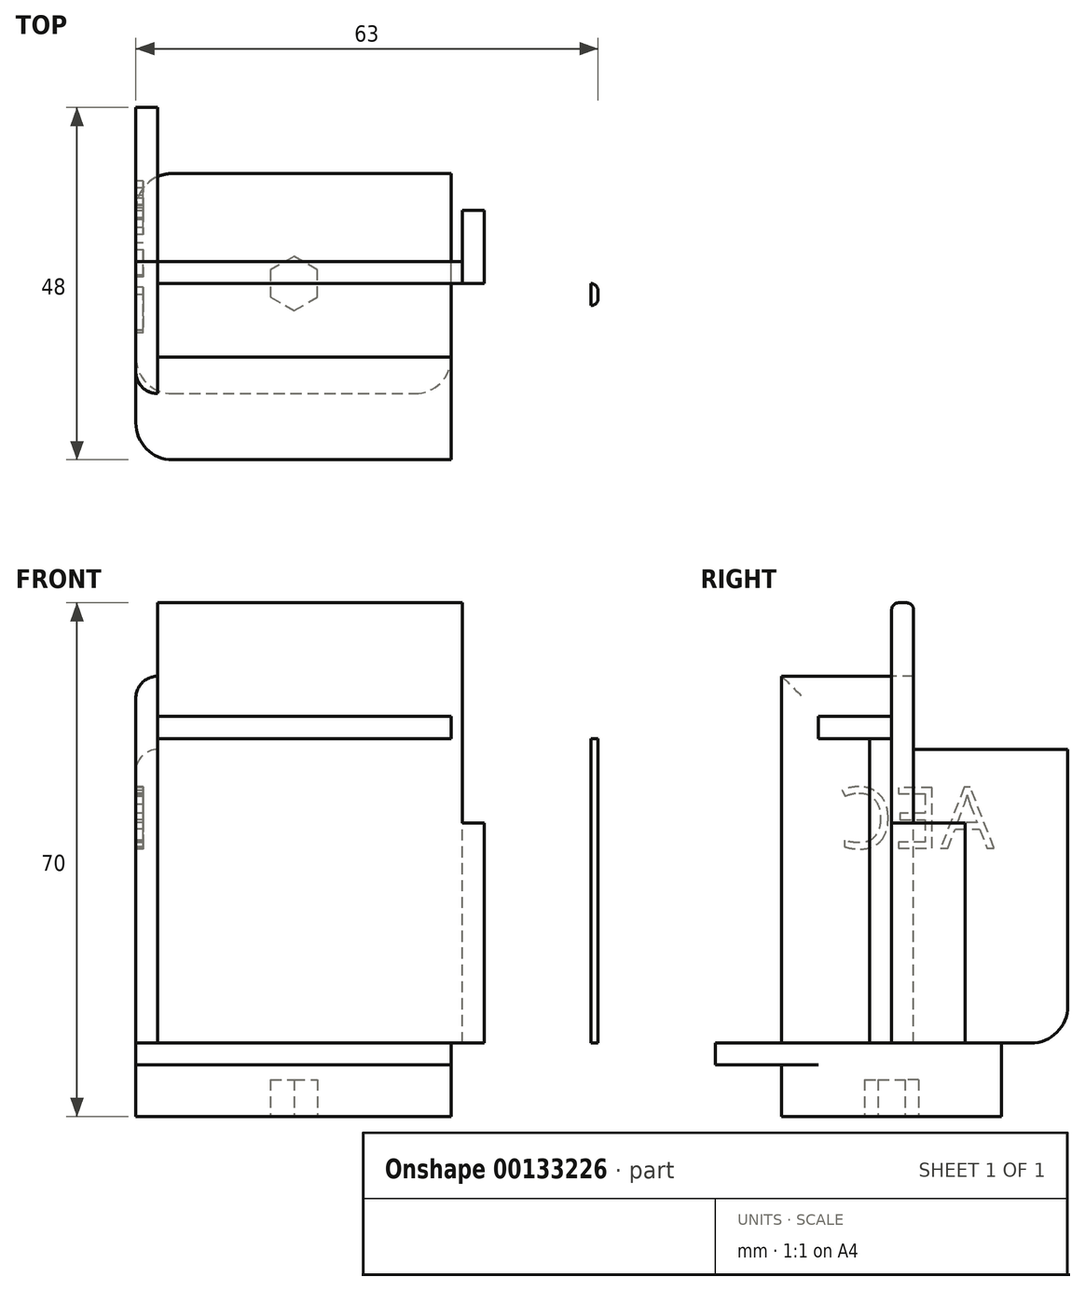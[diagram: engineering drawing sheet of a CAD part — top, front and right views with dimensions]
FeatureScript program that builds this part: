
annotation { "Feature Type Name" : "Feature", "Feature Type Description" : "" }
export const myFeature = defineFeature(function(context is Context, id is Id, definition is map)
    precondition{}
    {
        {
            var Q0;
            Q0=qCreatedBy(makeId("Front.planeOp"),FACE);
            var sketch = newSketch(context, id + "F0", { "sketchPlane" : qUnion([Q0])});
            skLineSegment(sketch, "E0.bottom", {"start": v(0, 0) * mm, "end": v(60, 0) * mm});
            skLineSegment(sketch, "E0.top", {"start": v(0, 41.5) * mm, "end": v(60, 41.5) * mm});
            skLineSegment(sketch, "E0.left", {"start": v(0, 0) * mm, "end": v(0, 41.5) * mm});
            skLineSegment(sketch, "E0.right", {"start": v(60, 0) * mm, "end": v(60, 41.5) * mm});
            skSolve(sketch);
        }
        {
            var Q0;
            Q0=makeQuery(id+"F0.imprint","IMPRINT",FACE,{"disambiguationData":[TD([[makeQuery(id+"F0.imprint","IMPRINT",EDGE,{"derivedFrom":sQuery(id+"F0.wireOp",EDGE,"E0.bottom")}),1.0]])]});
            extrude(context, id + "F1", {"entities" : qUnion([Q0]), "depth" : 3 * mm});
        }
        {
            var Q0;
            Q0=makeQuery(id+"F1.opExtrude","CAP_FACE",FACE,{"disambiguationData":[OSD([sQuery(id+"F0.wireOp",EDGE,"E0.bottom"),sQuery(id+"F0.wireOp",EDGE,"E0.top"),sQuery(id+"F0.wireOp",EDGE,"E0.left"),sQuery(id+"F0.wireOp",EDGE,"E0.right")])],"isStart":true});
            var sketch = newSketch(context, id + "F2", { "sketchPlane" : qUnion([Q0])});
            skLineSegment(sketch, "E1.bottom", {"start": v(0, 0) * mm, "end": v(-41.5, 0) * mm});
            skLineSegment(sketch, "E1.top", {"start": v(0, 60) * mm, "end": v(-41.5, 60) * mm});
            skLineSegment(sketch, "E1.left", {"start": v(0, 0) * mm, "end": v(0, 60) * mm});
            skLineSegment(sketch, "E1.right", {"start": v(-41.5, 0) * mm, "end": v(-41.5, 60) * mm});
            skSolve(sketch);
        }
        {
            var Q0;
            {var subQ0=sQuery(id+"F2.wireOp",EDGE,"E1.top");Q0=makeQuery(id+"F2.imprint","IMPRINT",FACE,{"disambiguationData":[TD([[makeQuery(id+"F2.imprint","IMPRINT",EDGE,{"derivedFrom":subQ0}),1.0]])]});}
            var Q1;
            {var subQ0=sQuery(id+"F2.wireOp",EDGE,"E1.bottom");Q1=makeQuery(id+"F2.imprint","IMPRINT",FACE,{"disambiguationData":[TD([[makeQuery(id+"F2.imprint","IMPRINT",EDGE,{"derivedFrom":subQ0}),-1.0]])]});}
            extrude(context, id + "F3", {"entities" : qUnion([Q0, Q1]), "operationType" : NewBodyOperationType.ADD, "depth" : 3 * mm});
        }
        {
            var Q0;
            Q0=makeQuery(id+"F3.boolean.opBoolean","MERGE",FACE,{"derivedFrom":[makeQuery(id+"F1.opExtrude","SWEPT_FACE",FACE,{"disambiguationData":[OSD([sQuery(id+"F0.wireOp",EDGE,"E0.left")])]}),makeQuery(id+"F3.opExtrude","SWEPT_FACE",FACE,{"disambiguationData":[OSD([sQuery(id+"F2.wireOp",EDGE,"E1.left")])]})]});
            var sketch = newSketch(context, id + "F4", { "sketchPlane" : qUnion([Q0])});
            skLineSegment(sketch, "E2", {"start": v(0, 0) * mm, "end": v(-15, 0) * mm, "construction": true});
            skLineSegment(sketch, "E3", {"start": v(-15, 0) * mm, "end": v(15, 0) * mm, "construction": true});
            skLineSegment(sketch, "E4", {"start": v(15, 0) * mm, "end": v(15, 50) * mm, "construction": true});
            skLineSegment(sketch, "E5.bottom", {"start": v(-15, 0) * mm, "end": v(15, 0) * mm});
            skLineSegment(sketch, "E5.top", {"start": v(-15, 50) * mm, "end": v(15, 50) * mm});
            skLineSegment(sketch, "E5.left", {"start": v(-15, 0) * mm, "end": v(-15, 50) * mm});
            skLineSegment(sketch, "E5.right", {"start": v(15, 0) * mm, "end": v(15, 50) * mm});
            skSolve(sketch);
        }
        {
            var Q0;
            {var subQ3=sQuery(id+"F4.wireOp",EDGE,"E5.left");Q0=makeQuery(id+"F4.imprint","IMPRINT",FACE,{"disambiguationData":[TD([[makeQuery(id+"F4.imprint","IMPRINT",EDGE,{"derivedFrom":subQ3}),-1.0]])]});}
            var Q1;
            {var subQ2=sQuery(id+"F4.wireOp",EDGE,"E5.right");Q1=makeQuery(id+"F4.imprint","IMPRINT",FACE,{"disambiguationData":[TD([[makeQuery(id+"F4.imprint","IMPRINT",EDGE,{"derivedFrom":subQ2}),1.0]])]});}
            var Q2;
            {var subQ0=sQuery(id+"F0.wireOp",EDGE,"E0.left");var subQ1=makeQuery(id+"F1.opExtrude","CAP_EDGE",EDGE,{"disambiguationData":[OSD([subQ0])],"isStart":false});Q2=makeQuery(id+"F4.imprint","IMPRINT",FACE,{"disambiguationData":[TD([[makeQuery(id+"F4.imprint","IMPRINT",EDGE,{"derivedFrom":subQ1}),1.0]])]});}
            extrude(context, id + "F5", {"entities" : qUnion([Q0, Q1, Q2]), "operationType" : NewBodyOperationType.ADD, "depth" : 3 * mm});
        }
        {
            var Q0;
            Q0=makeQuery(id+"F5.boolean.opBoolean","MERGE",FACE,{"derivedFrom":[makeQuery(id+"F3.boolean.opBoolean","MERGE",FACE,{"derivedFrom":[makeQuery(id+"F1.opExtrude","SWEPT_FACE",FACE,{"disambiguationData":[OSD([sQuery(id+"F0.wireOp",EDGE,"E0.bottom")])]}),makeQuery(id+"F3.opExtrude","SWEPT_FACE",FACE,{"disambiguationData":[OSD([sQuery(id+"F2.wireOp",EDGE,"E1.bottom")])]})]}),makeQuery(id+"F5.opExtrude","SWEPT_FACE",FACE,{"disambiguationData":[OSD([sQuery(id+"F4.wireOp",EDGE,"E5.bottom")])]})]});
            var sketch = newSketch(context, id + "F6", { "sketchPlane" : qUnion([Q0])});
            skLineSegment(sketch, "E6.bottom", {"start": v(-3, 15) * mm, "end": v(47, 15) * mm});
            skLineSegment(sketch, "E6.top", {"start": v(-3, -15) * mm, "end": v(47, -15) * mm});
            skLineSegment(sketch, "E6.left", {"start": v(-3, 15) * mm, "end": v(-3, -15) * mm});
            skLineSegment(sketch, "E6.right", {"start": v(47, 15) * mm, "end": v(47, -15) * mm});
            skSolve(sketch);
        }
        {
            var Q0;
            {var subQ0=sQuery(id+"F6.wireOp",EDGE,"E6.bottom");var subQ5=sQuery(id+"F6.wireOp",EDGE,"E6.right");var subQ6=makeQuery(id+"F6.imprint","INTERSECT",VERTEX,{"derivedFrom":[subQ0,subQ5]});Q0=makeQuery(id+"F6.imprint","IMPRINT",FACE,{"disambiguationData":[TD([[makeQuery(id+"F6.imprint","IMPRINT",EDGE,{"disambiguationData":[TD([[subQ6,-1.0]])],"derivedFrom":subQ5}),-1.0]])]});}
            var Q1;
            {var subQ0=sQuery(id+"F2.wireOp",EDGE,"E1.bottom");Q1=makeQuery(id+"F6.imprint","IMPRINT",FACE,{"disambiguationData":[TD([[makeQuery(id+"F6.imprint","IMPRINT",EDGE,{"derivedFrom":makeQuery(id+"F3.opExtrude","CAP_EDGE",EDGE,{"disambiguationData":[OSD([subQ0])],"isStart":false})}),-1.0]])]});}
            var Q2;
            {var subQ6=sQuery(id+"F6.wireOp",EDGE,"E6.left");Q2=makeQuery(id+"F6.imprint","IMPRINT",FACE,{"disambiguationData":[TD([[makeQuery(id+"F6.imprint","IMPRINT",EDGE,{"derivedFrom":subQ6}),-1.0]])]});}
            extrude(context, id + "F7", {"entities" : qUnion([Q0, Q1, Q2]), "operationType" : NewBodyOperationType.ADD, "depth" : 10 * mm});
        }
        {
            var Q0;
            Q0=makeQuery(id+"F7.boolean.opBoolean","MERGE",FACE,{"derivedFrom":[makeQuery(id+"F5.opExtrude","SWEPT_FACE",FACE,{"disambiguationData":[OSD([sQuery(id+"F4.wireOp",EDGE,"E5.right")])]}),makeQuery(id+"F7.opExtrude","SWEPT_FACE",FACE,{"disambiguationData":[OSD([sQuery(id+"F6.wireOp",EDGE,"E6.bottom")])]})]});
            var sketch = newSketch(context, id + "F8", { "sketchPlane" : qUnion([Q0])});
            skLineSegment(sketch, "E7.bottom", {"start": v(-3, 0) * mm, "end": v(47, 0) * mm});
            skLineSegment(sketch, "E7.top", {"start": v(-3, -3) * mm, "end": v(47, -3) * mm});
            skLineSegment(sketch, "E7.left", {"start": v(-3, 0) * mm, "end": v(-3, -3) * mm});
            skLineSegment(sketch, "E7.right", {"start": v(47, 0) * mm, "end": v(47, -3) * mm});
            skSolve(sketch);
        }
        {
            var Q0;
            Q0=makeQuery(id+"F8.imprint","IMPRINT",FACE,{"disambiguationData":[TD([[makeQuery(id+"F8.imprint","IMPRINT",EDGE,{"derivedFrom":sQuery(id+"F8.wireOp",EDGE,"E7.top")}),1.0]])]});
            extrude(context, id + "F9", {"entities" : qUnion([Q0]), "operationType" : NewBodyOperationType.ADD, "depth" : 9 * mm});
        }
        {
            var Q0;
            Q0=makeQuery(id+"F9.opExtrude","CAP_FACE",FACE,{"disambiguationData":[OSD([sQuery(id+"F8.wireOp",EDGE,"E7.bottom"),sQuery(id+"F8.wireOp",EDGE,"E7.top"),sQuery(id+"F8.wireOp",EDGE,"E7.left"),sQuery(id+"F8.wireOp",EDGE,"E7.right")])],"isStart":false});
            var sketch = newSketch(context, id + "F10", { "sketchPlane" : qUnion([Q0])});
            skLineSegment(sketch, "E8.bottom", {"start": v(22, -3) * mm, "end": v(47, -3) * mm});
            skLineSegment(sketch, "E8.top", {"start": v(22, 7) * mm, "end": v(47, 7) * mm});
            skLineSegment(sketch, "E8.left", {"start": v(22, -3) * mm, "end": v(22, 7) * mm});
            skLineSegment(sketch, "E8.right", {"start": v(47, -3) * mm, "end": v(47, 7) * mm});
            skSolve(sketch);
        }
        {
            var Q0;
            {var subQ0=sQuery(id+"F10.wireOp",EDGE,"E8.top");Q0=makeQuery(id+"F10.imprint","IMPRINT",FACE,{"disambiguationData":[TD([[makeQuery(id+"F10.imprint","IMPRINT",EDGE,{"derivedFrom":subQ0}),-1.0]])]});}
            var Q1;
            {var subQ0=sQuery(id+"F10.wireOp",EDGE,"E8.bottom");Q1=makeQuery(id+"F10.imprint","IMPRINT",FACE,{"disambiguationData":[TD([[makeQuery(id+"F10.imprint","IMPRINT",EDGE,{"derivedFrom":subQ0}),1.0]])]});}
            extrude(context, id + "F11", {"entities" : qUnion([Q0, Q1]), "operationType" : NewBodyOperationType.ADD, "depth" : 3 * mm});
        }
        {
            var Q0;
            Q0=makeQuery(id+"F11.opExtrude","CAP_FACE",FACE,{"disambiguationData":[OSD([sQuery(id+"F10.wireOp",EDGE,"E8.bottom"),sQuery(id+"F10.wireOp",EDGE,"E8.top"),sQuery(id+"F10.wireOp",EDGE,"E8.left"),sQuery(id+"F10.wireOp",EDGE,"E8.right")])],"isStart":false});
            var sketch = newSketch(context, id + "F12", { "sketchPlane" : qUnion([Q0])});
            skArc(sketch, "E9", {"start": v(17.11, 3.6) * mm, "mid": v(26.46, 3.05) * mm, "end": v(24.78, 12.26) * mm});
            skLineSegment(sketch, "E10", {"start": v(24.78, 12.26) * mm, "end": v(17.11, 3.6) * mm});
            skSolve(sketch);
        }
        {
            var Q0;
            {var subQ0=sQuery(id+"F12.wireOp",EDGE,"E9");var subQ1=makeQuery(id+"F11.opExtrude","CAP_EDGE",EDGE,{"disambiguationData":[OSD([sQuery(id+"F10.wireOp",EDGE,"E8.left")])],"isStart":false});var subQ2=makeQuery(id+"F12.imprint","INTERSECT",VERTEX,{"derivedFrom":[subQ1,subQ0]});Q0=makeQuery(id+"F12.imprint","IMPRINT",FACE,{"disambiguationData":[TD([[makeQuery(id+"F12.imprint","IMPRINT",EDGE,{"disambiguationData":[TD([[subQ2,-1.0]])],"derivedFrom":subQ0}),1.0]])]});}
            extrude(context, id + "F13", {"entities" : qUnion([Q0]), "operationType" : NewBodyOperationType.REMOVE, "oppositeDirection" : true, "depth" : 3 * mm});
        }
        {
            var Q0;
            Q0=makeQuery(id+"F11.boolean.opBoolean","MERGE",FACE,{"derivedFrom":[makeQuery(id+"F9.boolean.opBoolean","MERGE",FACE,{"derivedFrom":[makeQuery(id+"F7.opExtrude","SWEPT_FACE",FACE,{"disambiguationData":[OSD([sQuery(id+"F6.wireOp",EDGE,"E6.right")])]}),makeQuery(id+"F9.opExtrude","SWEPT_FACE",FACE,{"disambiguationData":[OSD([sQuery(id+"F8.wireOp",EDGE,"E7.right")])]})]}),makeQuery(id+"F11.opExtrude","SWEPT_FACE",FACE,{"disambiguationData":[OSD([sQuery(id+"F10.wireOp",EDGE,"E8.right")])]})]});
            var sketch = newSketch(context, id + "F14", { "sketchPlane" : qUnion([Q0])});
            skLineSegment(sketch, "E11.bottom", {"start": v(15, 0) * mm, "end": v(-27.93, 0) * mm});
            skLineSegment(sketch, "E11.top", {"start": v(15, -10) * mm, "end": v(-27.93, -10) * mm});
            skLineSegment(sketch, "E11.left", {"start": v(15, 0) * mm, "end": v(15, -10) * mm});
            skLineSegment(sketch, "E11.right", {"start": v(-27.93, 0) * mm, "end": v(-27.93, -10) * mm});
            skSolve(sketch);
        }
        {
            var Q0;
            {var subQ5=sQuery(id+"F14.wireOp",EDGE,"E11.left");Q0=makeQuery(id+"F14.imprint","IMPRINT",FACE,{"disambiguationData":[TD([[makeQuery(id+"F14.imprint","IMPRINT",EDGE,{"derivedFrom":subQ5}),1.0]])]});}
            var Q1;
            {var subQ3=sQuery(id+"F14.wireOp",EDGE,"E11.right");Q1=makeQuery(id+"F14.imprint","IMPRINT",FACE,{"disambiguationData":[TD([[makeQuery(id+"F14.imprint","IMPRINT",EDGE,{"derivedFrom":subQ3}),1.0]])]});}
            extrude(context, id + "F15", {"entities" : qUnion([Q0, Q1]), "operationType" : NewBodyOperationType.REMOVE, "oppositeDirection" : true, "depth" : 7 * mm});
        }
        {
            var Q0;
            Q0=makeQuery(id+"F11.boolean.opBoolean","MERGE",FACE,{"derivedFrom":[makeQuery(id+"F9.boolean.opBoolean","MERGE",FACE,{"derivedFrom":[makeQuery(id+"F7.opExtrude","SWEPT_FACE",FACE,{"disambiguationData":[OSD([sQuery(id+"F6.wireOp",EDGE,"E6.right")])]}),makeQuery(id+"F9.opExtrude","SWEPT_FACE",FACE,{"disambiguationData":[OSD([sQuery(id+"F8.wireOp",EDGE,"E7.right")])]})]}),makeQuery(id+"F11.opExtrude","SWEPT_FACE",FACE,{"disambiguationData":[OSD([sQuery(id+"F10.wireOp",EDGE,"E8.right")])]})]});
            var sketch = newSketch(context, id + "F16", { "sketchPlane" : qUnion([Q0])});
            skLineSegment(sketch, "E12.bottom", {"start": v(-31.9, 9.79) * mm, "end": v(-20.1, 9.79) * mm});
            skLineSegment(sketch, "E12.top", {"start": v(-31.9, -3.14) * mm, "end": v(-20.1, -3.14) * mm});
            skLineSegment(sketch, "E12.left", {"start": v(-31.9, 9.79) * mm, "end": v(-31.9, -3.14) * mm});
            skLineSegment(sketch, "E12.right", {"start": v(-20.1, 9.79) * mm, "end": v(-20.1, -3.14) * mm});
            skSolve(sketch);
        }
        {
            var Q0;
            {var subQ0=sQuery(id+"F10.wireOp",EDGE,"E8.right");Q0=makeQuery(id+"F16.imprint","IMPRINT",FACE,{"disambiguationData":[TD([[makeQuery(id+"F16.imprint","IMPRINT",EDGE,{"derivedFrom":makeQuery(id+"F11.opExtrude","CAP_EDGE",EDGE,{"disambiguationData":[OSD([subQ0])],"isStart":true})}),1.0]])]});}
            extrude(context, id + "F17", {"entities" : qUnion([Q0]), "operationType" : NewBodyOperationType.REMOVE, "oppositeDirection" : true, "depth" : 7 * mm});
        }
        {
            var Q0;
            Q0=makeQuery(id+"F11.opExtrude","CAP_FACE",FACE,{"disambiguationData":[OSD([sQuery(id+"F10.wireOp",EDGE,"E8.bottom"),sQuery(id+"F10.wireOp",EDGE,"E8.top"),sQuery(id+"F10.wireOp",EDGE,"E8.left"),sQuery(id+"F10.wireOp",EDGE,"E8.right")])],"isStart":false});
            var sketch = newSketch(context, id + "F18", { "sketchPlane" : qUnion([Q0])});
            skLineSegment(sketch, "E13.bottom", {"start": v(40, 7) * mm, "end": v(35.21, 7) * mm});
            skLineSegment(sketch, "E13.top", {"start": v(40, 2.28) * mm, "end": v(35.21, 2.28) * mm});
            skLineSegment(sketch, "E13.left", {"start": v(40, 7) * mm, "end": v(40, 2.28) * mm});
            skLineSegment(sketch, "E13.right", {"start": v(35.21, 7) * mm, "end": v(35.21, 2.28) * mm});
            skSolve(sketch);
        }
        {
            var Q0;
            Q0=makeQuery(id+"F18.imprint","IMPRINT",FACE,{"disambiguationData":[TD([[makeQuery(id+"F18.imprint","IMPRINT",EDGE,{"derivedFrom":sQuery(id+"F18.wireOp",EDGE,"E13.bottom")}),-1.0]])]});
            extrude(context, id + "F19", {"entities" : qUnion([Q0]), "operationType" : NewBodyOperationType.REMOVE, "oppositeDirection" : true, "depth" : 5 * mm});
        }
        {
            var Q0;
            Q0=makeQuery(id+"F1.opExtrude","SWEPT_FACE",FACE,{"disambiguationData":[OSD([sQuery(id+"F0.wireOp",EDGE,"E0.top")])]});
            var sketch = newSketch(context, id + "F20", { "sketchPlane" : qUnion([Q0])});
            skLineSegment(sketch, "E14.bottom", {"start": v(0, 0) * mm, "end": v(40, 0) * mm});
            skLineSegment(sketch, "E14.top", {"start": v(0, -10) * mm, "end": v(40, -10) * mm});
            skLineSegment(sketch, "E14.left", {"start": v(0, 0) * mm, "end": v(0, -10) * mm});
            skLineSegment(sketch, "E14.right", {"start": v(40, 0) * mm, "end": v(40, -10) * mm});
            skSolve(sketch);
        }
        {
            var Q0;
            {var subQ0=sQuery(id+"F20.wireOp",EDGE,"E14.top");Q0=makeQuery(id+"F20.imprint","IMPRINT",FACE,{"disambiguationData":[TD([[makeQuery(id+"F20.imprint","IMPRINT",EDGE,{"derivedFrom":subQ0}),1.0]])]});}
            var Q1;
            {var subQ0=sQuery(id+"F20.wireOp",EDGE,"E14.bottom");Q1=makeQuery(id+"F20.imprint","IMPRINT",FACE,{"disambiguationData":[TD([[makeQuery(id+"F20.imprint","IMPRINT",EDGE,{"derivedFrom":subQ0}),-1.0]])]});}
            extrude(context, id + "F21", {"entities" : qUnion([Q0, Q1]), "operationType" : NewBodyOperationType.ADD, "depth" : 3 * mm});
        }
        {
            var Q0;
            Q0=makeQuery(id+"F3.opExtrude","SWEPT_FACE",FACE,{"disambiguationData":[OSD([sQuery(id+"F2.wireOp",EDGE,"E1.right")])]});
            var sketch = newSketch(context, id + "F22", { "sketchPlane" : qUnion([Q0])});
            skLineSegment(sketch, "E15.bottom", {"start": v(0, 0) * mm, "end": v(10, 0) * mm});
            skLineSegment(sketch, "E15.top", {"start": v(0, 30) * mm, "end": v(10, 30) * mm});
            skLineSegment(sketch, "E15.left", {"start": v(0, 0) * mm, "end": v(0, 30) * mm});
            skLineSegment(sketch, "E15.right", {"start": v(10, 0) * mm, "end": v(10, 30) * mm});
            skSolve(sketch);
        }
        {
            var Q0;
            {var subQ3=sQuery(id+"F22.wireOp",EDGE,"E15.right");Q0=makeQuery(id+"F22.imprint","IMPRINT",FACE,{"disambiguationData":[TD([[makeQuery(id+"F22.imprint","IMPRINT",EDGE,{"derivedFrom":subQ3}),1.0]])]});}
            var Q1;
            {var subQ4=sQuery(id+"F22.wireOp",EDGE,"E15.left");Q1=makeQuery(id+"F22.imprint","IMPRINT",FACE,{"disambiguationData":[TD([[makeQuery(id+"F22.imprint","IMPRINT",EDGE,{"derivedFrom":subQ4}),-1.0]])]});}
            extrude(context, id + "F23", {"entities" : qUnion([Q0, Q1]), "operationType" : NewBodyOperationType.ADD, "depth" : 3 * mm});
        }
        {
            var Q0;
            Q0=makeQuery(id+"F7.boolean.opBoolean","MERGE",FACE,{"derivedFrom":[makeQuery(id+"F5.opExtrude","SWEPT_FACE",FACE,{"disambiguationData":[OSD([sQuery(id+"F4.wireOp",EDGE,"E5.left")])]}),makeQuery(id+"F7.opExtrude","SWEPT_FACE",FACE,{"disambiguationData":[OSD([sQuery(id+"F6.wireOp",EDGE,"E6.top")])]})]});
            var sketch = newSketch(context, id + "F24", { "sketchPlane" : qUnion([Q0])});
            skLineSegment(sketch, "E16.bottom", {"start": v(0, 50) * mm, "end": v(3, 50) * mm});
            skLineSegment(sketch, "E16.top", {"start": v(0, 0) * mm, "end": v(3, 0) * mm});
            skLineSegment(sketch, "E16.left", {"start": v(0, 50) * mm, "end": v(0, 0) * mm});
            skLineSegment(sketch, "E16.right", {"start": v(3, 50) * mm, "end": v(3, 0) * mm});
            skSolve(sketch);
        }
        {
            var Q0;
            Q0=makeQuery(id+"F24.imprint","IMPRINT",FACE,{"disambiguationData":[TD([[makeQuery(id+"F24.imprint","IMPRINT",EDGE,{"derivedFrom":sQuery(id+"F24.wireOp",EDGE,"E16.bottom")}),1.0]])]});
            extrude(context, id + "F25", {"entities" : qUnion([Q0]), "operationType" : NewBodyOperationType.ADD, "depth" : 9 * mm});
        }
        {
            var Q0;
            Q0=makeQuery(id+"F11.opExtrude","CAP_FACE",FACE,{"disambiguationData":[OSD([sQuery(id+"F10.wireOp",EDGE,"E8.bottom"),sQuery(id+"F10.wireOp",EDGE,"E8.top"),sQuery(id+"F10.wireOp",EDGE,"E8.left"),sQuery(id+"F10.wireOp",EDGE,"E8.right")])],"isStart":false});
            var sketch = newSketch(context, id + "F26", { "sketchPlane" : qUnion([Q0])});
            skLineSegment(sketch, "E17.bottom", {"start": v(27.95, 7) * mm, "end": v(22, 7) * mm});
            skLineSegment(sketch, "E17.top", {"start": v(27.95, 1.05) * mm, "end": v(22, 1.05) * mm});
            skLineSegment(sketch, "E17.left", {"start": v(27.95, 7) * mm, "end": v(27.95, 1.05) * mm});
            skLineSegment(sketch, "E17.right", {"start": v(22, 7) * mm, "end": v(22, 1.05) * mm});
            skSolve(sketch);
        }
        {
            var Q0;
            Q0=makeQuery(id+"F26.imprint","IMPRINT",FACE,{"disambiguationData":[TD([[makeQuery(id+"F26.imprint","IMPRINT",EDGE,{"derivedFrom":sQuery(id+"F26.wireOp",EDGE,"E17.top")}),-1.0]])]});
            extrude(context, id + "F27", {"entities" : qUnion([Q0]), "operationType" : NewBodyOperationType.REMOVE, "oppositeDirection" : true, "depth" : 5 * mm});
        }
        {
            var Q0;
            Q0=makeQuery(id+"F25.opExtrude","CAP_FACE",FACE,{"disambiguationData":[OSD([sQuery(id+"F24.wireOp",EDGE,"E16.bottom"),sQuery(id+"F24.wireOp",EDGE,"E16.top"),sQuery(id+"F24.wireOp",EDGE,"E16.left"),sQuery(id+"F24.wireOp",EDGE,"E16.right")])],"isStart":false});
            var sketch = newSketch(context, id + "F28", { "sketchPlane" : qUnion([Q0])});
            skLineSegment(sketch, "E18", {"start": v(0, 0) * mm, "end": v(0, 40) * mm, "construction": true});
            skLineSegment(sketch, "E19", {"start": v(0, 40) * mm, "end": v(-9.05, 40) * mm, "construction": true});
            skLineSegment(sketch, "E20.bottom", {"start": v(0, 40) * mm, "end": v(5.6, 40) * mm, "construction": true});
            skLineSegment(sketch, "E20.top", {"start": v(0, 52.74) * mm, "end": v(5.6, 52.74) * mm, "construction": true});
            skLineSegment(sketch, "E20.left", {"start": v(0, 40) * mm, "end": v(0, 52.74) * mm, "construction": true});
            skLineSegment(sketch, "E20.right", {"start": v(5.6, 40) * mm, "end": v(5.6, 52.74) * mm, "construction": true});
            skLineSegment(sketch, "E21.bottom", {"start": v(0, 40) * mm, "end": v(5.6, 40) * mm});
            skLineSegment(sketch, "E21.top", {"start": v(0, 52.74) * mm, "end": v(5.6, 52.74) * mm});
            skLineSegment(sketch, "E21.left", {"start": v(0, 40) * mm, "end": v(0, 52.74) * mm});
            skLineSegment(sketch, "E21.right", {"start": v(5.6, 40) * mm, "end": v(5.6, 52.74) * mm});
            skSolve(sketch);
        }
        {
            var Q0;
            {var subQ5=makeQuery(id+"F25.opExtrude","CAP_EDGE",EDGE,{"disambiguationData":[OSD([sQuery(id+"F24.wireOp",EDGE,"E16.bottom")])],"isStart":false});Q0=makeQuery(id+"F28.imprint","IMPRINT",FACE,{"disambiguationData":[TD([[makeQuery(id+"F28.imprint","IMPRINT",EDGE,{"derivedFrom":subQ5}),1.0]])]});}
            extrude(context, id + "F29", {"entities" : qUnion([Q0]), "operationType" : NewBodyOperationType.REMOVE, "oppositeDirection" : true, "depth" : 21 * mm});
        }
        {
            var Q0;
            Q0=makeQuery(id+"F25.opExtrude","CAP_FACE",FACE,{"disambiguationData":[OSD([sQuery(id+"F24.wireOp",EDGE,"E16.bottom"),sQuery(id+"F24.wireOp",EDGE,"E16.top"),sQuery(id+"F24.wireOp",EDGE,"E16.left"),sQuery(id+"F24.wireOp",EDGE,"E16.right")])],"isStart":false});
            var sketch = newSketch(context, id + "F30", { "sketchPlane" : qUnion([Q0])});
            skLineSegment(sketch, "E22", {"start": v(0, 0) * mm, "end": v(3, 0) * mm, "construction": true});
            skLineSegment(sketch, "E23", {"start": v(3, 0) * mm, "end": v(3, 40) * mm, "construction": true});
            skLineSegment(sketch, "E24.left", {"start": v(3, 40) * mm, "end": v(3, 22) * mm});
            skLineSegment(sketch, "E24.right", {"start": v(-7.41, 35.3) * mm, "end": v(-7.41, 26.8) * mm});
            skLineSegment(sketch, "E25.top", {"start": v(-7.41, 35.3) * mm, "end": v(-2.71, 35.3) * mm});
            skLineSegment(sketch, "E25.right", {"start": v(-2.71, 40) * mm, "end": v(-2.71, 35.3) * mm});
            skLineSegment(sketch, "E26.top", {"start": v(-7.41, 26.8) * mm, "end": v(-1.51, 26.8) * mm});
            skLineSegment(sketch, "E26.right", {"start": v(-1.51, 22) * mm, "end": v(-1.51, 26.8) * mm});
            skLineSegment(sketch, "E27", {"start": v(-2.71, 40) * mm, "end": v(3, 40) * mm});
            skLineSegment(sketch, "E28", {"start": v(-1.51, 22) * mm, "end": v(3, 22) * mm});
            skSolve(sketch);
        }
        {
            var Q0;
            {var subQ0=sQuery(id+"F30.wireOp",EDGE,"E24.left");Q0=makeQuery(id+"F30.imprint","IMPRINT",FACE,{"disambiguationData":[TD([[makeQuery(id+"F30.imprint","IMPRINT",EDGE,{"derivedFrom":subQ0}),1.0]])]});}
            var Q1;
            Q1=makeQuery(id+"F30.imprint","IMPRINT",FACE,{"disambiguationData":[TD([[makeQuery(id+"F30.imprint","IMPRINT",EDGE,{"derivedFrom":sQuery(id+"F30.wireOp",EDGE,"E24.right")}),1.0]])]});
            extrude(context, id + "F31", {"entities" : qUnion([Q0, Q1]), "operationType" : NewBodyOperationType.ADD, "depth" : 3 * mm});
        }
        {
            var Q0;
            Q0=makeQuery(id+"F31.opExtrude","CAP_EDGE",EDGE,{"disambiguationData":[OSD([sQuery(id+"F30.wireOp",EDGE,"E24.right")])],"isStart":false});
            fillet(context, id + "F32", {"entities" : qUnion([Q0]), "radius" : 1 * mm, "tangentPropagation" : true, "allowEdgeOverflow" : false});
        }
        {
            var Q0;
            Q0=makeQuery(id+"F31.opExtrude","CAP_EDGE",EDGE,{"disambiguationData":[OSD([sQuery(id+"F30.wireOp",EDGE,"E25.top")])],"isStart":false});
            var Q1;
            Q1=makeQuery(id+"F31.opExtrude","CAP_EDGE",EDGE,{"disambiguationData":[OSD([sQuery(id+"F30.wireOp",EDGE,"E26.top")])],"isStart":false});
            var Q2;
            Q2=makeQuery(id+"F31.opExtrude","CAP_EDGE",EDGE,{"disambiguationData":[OSD([sQuery(id+"F30.wireOp",EDGE,"E26.right")])],"isStart":false});
            var Q3;
            Q3=makeQuery(id+"F31.opExtrude","CAP_EDGE",EDGE,{"disambiguationData":[OSD([sQuery(id+"F30.wireOp",EDGE,"E25.right")])],"isStart":false});
            fillet(context, id + "F33", {"entities" : qUnion([Q0, Q1, Q2, Q3]), "radius" : 1 * mm, "tangentPropagation" : true, "allowEdgeOverflow" : false});
        }
        {
            var Q0;
            Q0=makeQuery(id+"F25.opExtrude","CAP_EDGE",EDGE,{"disambiguationData":[OSD([sQuery(id+"F24.wireOp",EDGE,"E16.top")])],"isStart":false});
            fillet(context, id + "F34", {"entities" : qUnion([Q0]), "radius" : 5 * mm, "tangentPropagation" : true, "allowEdgeOverflow" : false});
        }
        {
            var Q0;
            Q0=makeQuery(id+"F19.boolean.opBoolean","COPY",EDGE,{"derivedFrom":makeQuery(id+"F19.opExtrude","CAP_EDGE",EDGE,{"disambiguationData":[OSD([sQuery(id+"F18.wireOp",EDGE,"E13.right")])],"isStart":true})});
            var Q1;
            Q1=makeQuery(id+"F19.boolean.opBoolean","COPY",EDGE,{"derivedFrom":makeQuery(id+"F19.opExtrude","CAP_EDGE",EDGE,{"disambiguationData":[OSD([sQuery(id+"F18.wireOp",EDGE,"E13.top")])],"isStart":true})});
            var Q2;
            Q2=makeQuery(id+"F11.opExtrude","CAP_EDGE",EDGE,{"disambiguationData":[OSD([sQuery(id+"F10.wireOp",EDGE,"E8.top")])],"isStart":false});
            var Q3;
            Q3=makeQuery(id+"F27.boolean.opBoolean","COPY",EDGE,{"derivedFrom":makeQuery(id+"F27.opExtrude","CAP_EDGE",EDGE,{"disambiguationData":[OSD([sQuery(id+"F26.wireOp",EDGE,"E17.left")])],"isStart":true})});
            var Q4;
            Q4=makeQuery(id+"F27.boolean.opBoolean","COPY",EDGE,{"derivedFrom":makeQuery(id+"F27.opExtrude","CAP_EDGE",EDGE,{"disambiguationData":[OSD([sQuery(id+"F26.wireOp",EDGE,"E17.top")])],"isStart":true})});
            fillet(context, id + "F35", {"entities" : qUnion([Q0, Q1, Q2, Q3, Q4]), "radius" : 1 * mm, "tangentPropagation" : true, "allowEdgeOverflow" : false});
        }
        {
            var Q0;
            Q0=makeQuery(id+"F9.opExtrude","CAP_EDGE",EDGE,{"disambiguationData":[OSD([sQuery(id+"F8.wireOp",EDGE,"E7.left")])],"isStart":false});
            fillet(context, id + "F36", {"entities" : qUnion([Q0]), "radius" : 5 * mm, "tangentPropagation" : true, "allowEdgeOverflow" : false});
        }
        {
            var Q0;
            Q0=makeQuery(id+"F1.opExtrude","CAP_EDGE",EDGE,{"disambiguationData":[OSD([sQuery(id+"F0.wireOp",EDGE,"E0.right")])],"isStart":false});
            var Q1;
            Q1=makeQuery(id+"F1.opExtrude","CAP_EDGE",EDGE,{"disambiguationData":[OSD([sQuery(id+"F0.wireOp",EDGE,"E0.right")])],"isStart":true});
            fillet(context, id + "F37", {"entities" : qUnion([Q0, Q1]), "radius" : 1 * mm, "tangentPropagation" : true, "allowEdgeOverflow" : false});
        }
        {
            var Q0;
            Q0=makeQuery(id+"F3.opExtrude","CAP_EDGE",EDGE,{"disambiguationData":[OSD([sQuery(id+"F2.wireOp",EDGE,"E1.top")])],"isStart":false});
            var Q1;
            Q1=makeQuery(id+"F3.opExtrude","CAP_EDGE",EDGE,{"disambiguationData":[OSD([sQuery(id+"F2.wireOp",EDGE,"E1.top")])],"isStart":true});
            fillet(context, id + "F38", {"entities" : qUnion([Q0, Q1]), "radius" : 1 * mm, "tangentPropagation" : true, "allowEdgeOverflow" : false});
        }
        {
            var Q0;
            Q0=makeQuery(id+"F15.boolean.opBoolean","COPY",EDGE,{"derivedFrom":makeQuery(id+"F15.opExtrude","CAP_EDGE",EDGE,{"disambiguationData":[OSD([sQuery(id+"F14.wireOp",EDGE,"E11.left")])],"isStart":false})});
            var Q1;
            {var subQ0=sQuery(id+"F6.wireOp",EDGE,"E6.right");var subQ2=sQuery(id+"F6.wireOp",EDGE,"E6.bottom");var subQ3=sQuery(id+"F4.wireOp",EDGE,"E5.right");Q1=makeQuery(id+"F15.boolean.opBoolean","INTERSECT",EDGE,{"derivedFrom":[makeQuery(id+"F9.boolean.opBoolean","SPLIT",FACE,{"disambiguationData":[TD([makeQuery(id+"F7.opExtrude","SWEPT_FACE",FACE,{"disambiguationData":[OSD([subQ0])]})])],"derivedFrom":makeQuery(id+"F7.boolean.opBoolean","MERGE",FACE,{"derivedFrom":[makeQuery(id+"F5.opExtrude","SWEPT_FACE",FACE,{"disambiguationData":[OSD([subQ3])]}),makeQuery(id+"F7.opExtrude","SWEPT_FACE",FACE,{"disambiguationData":[OSD([subQ2])]})]})}),makeQuery(id+"F15.opExtrude","CAP_FACE",FACE,{"disambiguationData":[OSD([sQuery(id+"F14.wireOp",EDGE,"E11.bottom"),sQuery(id+"F14.wireOp",EDGE,"E11.top"),sQuery(id+"F14.wireOp",EDGE,"E11.left"),sQuery(id+"F14.wireOp",EDGE,"E11.right")])],"isStart":false})]});}
            var Q2;
            Q2=makeQuery(id+"F7.boolean.opBoolean","MERGE",EDGE,{"derivedFrom":[makeQuery(id+"F5.opExtrude","CAP_EDGE",EDGE,{"disambiguationData":[OSD([sQuery(id+"F4.wireOp",EDGE,"E5.left")])],"isStart":false}),makeQuery(id+"F7.opExtrude","SWEPT_EDGE",EDGE,{"disambiguationData":[OSD([sQuery(id+"F6.wireOp",EDGE,"E6.top"),sQuery(id+"F6.wireOp",EDGE,"E6.left")])]})]});
            var Q3;
            {var subQ0=sQuery(id+"F6.wireOp",EDGE,"E6.left");var subQ1=sQuery(id+"F6.wireOp",EDGE,"E6.bottom");var subQ2=sQuery(id+"F4.wireOp",EDGE,"E5.right");Q3=makeQuery(id+"F9.boolean.opBoolean","SPLIT",EDGE,{"disambiguationData":[TD([makeQuery(id+"F9.opExtrude","SWEPT_FACE",FACE,{"disambiguationData":[OSD([sQuery(id+"F8.wireOp",EDGE,"E7.top")])]})])],"derivedFrom":makeQuery(id+"F7.boolean.opBoolean","MERGE",EDGE,{"derivedFrom":[makeQuery(id+"F5.opExtrude","CAP_EDGE",EDGE,{"disambiguationData":[OSD([subQ2])],"isStart":false}),makeQuery(id+"F7.opExtrude","SWEPT_EDGE",EDGE,{"disambiguationData":[OSD([subQ1,subQ0])]})]})});}
            fillet(context, id + "F39", {"entities" : qUnion([Q0, Q1, Q2, Q3]), "radius" : 5 * mm, "tangentPropagation" : true, "allowEdgeOverflow" : false});
        }
        {
            var Q0;
            Q0=makeQuery(id+"F31.boolean.opBoolean","MERGE",FACE,{"derivedFrom":[makeQuery(id+"F25.boolean.opBoolean","MERGE",FACE,{"derivedFrom":[makeQuery(id+"F9.boolean.opBoolean","MERGE",FACE,{"derivedFrom":[makeQuery(id+"F7.boolean.opBoolean","MERGE",FACE,{"derivedFrom":[makeQuery(id+"F5.opExtrude","CAP_FACE",FACE,{"disambiguationData":[OSD([sQuery(id+"F4.wireOp",EDGE,"E5.bottom"),sQuery(id+"F4.wireOp",EDGE,"E5.top"),sQuery(id+"F4.wireOp",EDGE,"E5.left"),sQuery(id+"F4.wireOp",EDGE,"E5.right")])],"isStart":false}),makeQuery(id+"F7.opExtrude","SWEPT_FACE",FACE,{"disambiguationData":[OSD([sQuery(id+"F6.wireOp",EDGE,"E6.left")])]})]}),makeQuery(id+"F9.opExtrude","SWEPT_FACE",FACE,{"disambiguationData":[OSD([sQuery(id+"F8.wireOp",EDGE,"E7.left")])]})]}),makeQuery(id+"F25.opExtrude","SWEPT_FACE",FACE,{"disambiguationData":[OSD([sQuery(id+"F24.wireOp",EDGE,"E16.right")])]})]}),makeQuery(id+"F31.opExtrude","SWEPT_FACE",FACE,{"disambiguationData":[OSD([sQuery(id+"F30.wireOp",EDGE,"E24.left")])]})]});
            var sketch = newSketch(context, id + "F40", { "sketchPlane" : qUnion([Q0])});
            skText(sketch, "E29", { "text": "AEC", "fontName": "OpenSans-Regular.ttf"});
            const initialGuessF40  = {"E29": [-0.01398, 0.02655, 1, 0, 0.00833]};
            skSetInitialGuess(sketch, initialGuessF40);
            skSolve(sketch);
        }
        {
            var Q0;
            Q0 = qSketchRegion(id + "F40", true);
            extrude(context, id + "F41", {"entities" : qUnion([Q0]), "operationType" : NewBodyOperationType.REMOVE, "oppositeDirection" : true, "depth" : 1 * mm});
        }
        {
            var Q0;
            Q0=makeQuery(id+"F7.opExtrude","CAP_FACE",FACE,{"disambiguationData":[OSD([sQuery(id+"F6.wireOp",EDGE,"E6.bottom"),sQuery(id+"F6.wireOp",EDGE,"E6.top"),sQuery(id+"F6.wireOp",EDGE,"E6.left"),sQuery(id+"F6.wireOp",EDGE,"E6.right")])],"isStart":false});
            var sketch = newSketch(context, id + "F42", { "sketchPlane" : qUnion([Q0])});
            skCircle(sketch, "E30.cCircle", {"center": v(18.55, 0) * mm, "radius": 3.2 * mm, "construction": true});
            skLineSegment(sketch, "E30.0", {"start": v(21.75, 1.85) * mm, "end": v(21.75, -1.85) * mm});
            skLineSegment(sketch, "E30.1", {"start": v(21.75, -1.85) * mm, "end": v(18.55, -3.7) * mm});
            skLineSegment(sketch, "E30.2", {"start": v(18.55, -3.7) * mm, "end": v(15.35, -1.85) * mm});
            skLineSegment(sketch, "E30.3", {"start": v(15.35, -1.85) * mm, "end": v(15.35, 1.85) * mm});
            skLineSegment(sketch, "E30.4", {"start": v(15.35, 1.85) * mm, "end": v(18.55, 3.7) * mm});
            skLineSegment(sketch, "E30.5", {"start": v(18.55, 3.7) * mm, "end": v(21.75, 1.85) * mm});
            skPoint(sketch, "E30.0.midPoint", {"position": v(21.75, 0) * mm});
            skSolve(sketch);
        }
        {
            var Q0;
            Q0=makeQuery(id+"F42.imprint","IMPRINT",FACE,{"disambiguationData":[TD([[makeQuery(id+"F42.imprint","IMPRINT",EDGE,{"derivedFrom":sQuery(id+"F42.wireOp",EDGE,"E30.0")}),-1.0]])]});
            extrude(context, id + "F43", {"entities" : qUnion([Q0]), "operationType" : NewBodyOperationType.REMOVE, "oppositeDirection" : true, "depth" : 5 * mm});
        }
        {
            var Q0;
            Q0=makeQuery(id+"F9.opExtrude","CAP_FACE",FACE,{"disambiguationData":[OSD([sQuery(id+"F8.wireOp",EDGE,"E7.bottom"),sQuery(id+"F8.wireOp",EDGE,"E7.top"),sQuery(id+"F8.wireOp",EDGE,"E7.left"),sQuery(id+"F8.wireOp",EDGE,"E7.right")])],"isStart":false});
            var sketch = newSketch(context, id + "F44", { "sketchPlane" : qUnion([Q0])});
            skLineSegment(sketch, "E31.bottom", {"start": v(17.1, 10.52) * mm, "end": v(46.84, 10.52) * mm});
            skLineSegment(sketch, "E31.top", {"start": v(17.1, -7.16) * mm, "end": v(46.84, -7.16) * mm});
            skLineSegment(sketch, "E31.left", {"start": v(17.1, 10.52) * mm, "end": v(17.1, -7.16) * mm});
            skLineSegment(sketch, "E31.right", {"start": v(46.84, 10.52) * mm, "end": v(46.84, -7.16) * mm});
            skSolve(sketch);
        }
        {
            var Q0;
            {var subQ1=sQuery(id+"F44.wireOp",EDGE,"E31.bottom");Q0=makeQuery(id+"F44.imprint","IMPRINT",FACE,{"disambiguationData":[TD([[makeQuery(id+"F44.imprint","IMPRINT",EDGE,{"derivedFrom":subQ1}),-1.0]])]});}
            extrude(context, id + "F45", {"entities" : qUnion([Q0]), "operationType" : NewBodyOperationType.REMOVE, "depth" : 25 * mm});
        }
        {
            var Q0;
            Q0=makeQuery(id+"F25.opExtrude","CAP_FACE",FACE,{"disambiguationData":[OSD([sQuery(id+"F24.wireOp",EDGE,"E16.bottom"),sQuery(id+"F24.wireOp",EDGE,"E16.top"),sQuery(id+"F24.wireOp",EDGE,"E16.left"),sQuery(id+"F24.wireOp",EDGE,"E16.right")])],"isStart":false});
            var sketch = newSketch(context, id + "F46", { "sketchPlane" : qUnion([Q0])});
            skLineSegment(sketch, "E32.bottom", {"start": v(-11.73, 42.88) * mm, "end": v(14.08, 42.88) * mm});
            skLineSegment(sketch, "E32.top", {"start": v(-11.73, 19.17) * mm, "end": v(14.08, 19.17) * mm});
            skLineSegment(sketch, "E32.left", {"start": v(-11.73, 42.88) * mm, "end": v(-11.73, 19.17) * mm});
            skLineSegment(sketch, "E32.right", {"start": v(14.08, 42.88) * mm, "end": v(14.08, 19.17) * mm});
            skSolve(sketch);
        }
        {
            var Q0;
            Q0=makeQuery(id+"F46.imprint","IMPRINT",FACE,{"disambiguationData":[TD([[makeQuery(id+"F46.imprint","IMPRINT",EDGE,{"derivedFrom":sQuery(id+"F46.wireOp",EDGE,"E32.bottom")}),-1.0]])]});
            extrude(context, id + "F47", {"entities" : qUnion([Q0]), "operationType" : NewBodyOperationType.REMOVE, "depth" : 25 * mm});
        }
        {
            var Q0;
            Q0=makeQuery(id+"F25.boolean.opBoolean","MERGE",EDGE,{"derivedFrom":[makeQuery(id+"F5.opExtrude","CAP_EDGE",EDGE,{"disambiguationData":[OSD([sQuery(id+"F4.wireOp",EDGE,"E5.top")])],"isStart":false}),makeQuery(id+"F25.opExtrude","SWEPT_EDGE",EDGE,{"disambiguationData":[OSD([sQuery(id+"F24.wireOp",EDGE,"E16.bottom"),sQuery(id+"F24.wireOp",EDGE,"E16.right")])]})]});
            var Q1;
            Q1=makeQuery(id+"F29.boolean.opBoolean","COPY",EDGE,{"derivedFrom":makeQuery(id+"F29.opExtrude","CAP_EDGE",EDGE,{"disambiguationData":[OSD([sQuery(id+"F24.wireOp",EDGE,"E16.right")])],"isStart":false})});
            var Q2;
            Q2=makeQuery(id+"F31.boolean.opBoolean","MERGE",EDGE,{"derivedFrom":[makeQuery(id+"F29.boolean.opBoolean","COPY",EDGE,{"derivedFrom":makeQuery(id+"F29.opExtrude","SWEPT_EDGE",EDGE,{"disambiguationData":[OSD([sQuery(id+"F24.wireOp",EDGE,"E16.right"),sQuery(id+"F28.wireOp",EDGE,"E21.bottom")])]})}),makeQuery(id+"F31.opExtrude","SWEPT_EDGE",EDGE,{"disambiguationData":[OSD([sQuery(id+"F30.wireOp",EDGE,"E24.left"),sQuery(id+"F30.wireOp",EDGE,"E27")])]})]});
            var Q3;
            {var subQ0=sQuery(id+"F6.wireOp",EDGE,"E6.bottom");var subQ1=sQuery(id+"F4.wireOp",EDGE,"E5.right");var subQ2=sQuery(id+"F4.wireOp",EDGE,"E5.top");var subQ3=sQuery(id+"F6.wireOp",EDGE,"E6.left");Q3=makeQuery(id+"F9.boolean.opBoolean","SPLIT",EDGE,{"disambiguationData":[TD([makeQuery(id+"F5.opExtrude","SWEPT_FACE",FACE,{"disambiguationData":[OSD([subQ2])]})])],"derivedFrom":makeQuery(id+"F7.boolean.opBoolean","MERGE",EDGE,{"derivedFrom":[makeQuery(id+"F5.opExtrude","CAP_EDGE",EDGE,{"disambiguationData":[OSD([subQ1])],"isStart":false}),makeQuery(id+"F7.opExtrude","SWEPT_EDGE",EDGE,{"disambiguationData":[OSD([subQ0,subQ3])]})]})});}
            fillet(context, id + "F48", {"entities" : qUnion([Q0, Q1, Q2, Q3]), "radius" : 3 * mm, "tangentPropagation" : true, "allowEdgeOverflow" : false});
        }
        {
            var Q0;
            Q0=makeQuery(id+"F1.opExtrude","CAP_FACE",FACE,{"disambiguationData":[OSD([sQuery(id+"F0.wireOp",EDGE,"E0.bottom"),sQuery(id+"F0.wireOp",EDGE,"E0.top"),sQuery(id+"F0.wireOp",EDGE,"E0.left"),sQuery(id+"F0.wireOp",EDGE,"E0.right")])],"isStart":false});
            var sketch = newSketch(context, id + "F49", { "sketchPlane" : qUnion([Q0])});
            skLineSegment(sketch, "E33.bottom", {"start": v(0, 0) * mm, "end": v(65.18, 0) * mm});
            skLineSegment(sketch, "E33.top", {"start": v(0, 41.5) * mm, "end": v(65.18, 41.5) * mm});
            skLineSegment(sketch, "E33.left", {"start": v(0, 0) * mm, "end": v(0, 41.5) * mm});
            skLineSegment(sketch, "E33.right", {"start": v(65.18, 0) * mm, "end": v(65.18, 41.5) * mm});
            skSolve(sketch);
        }
        {
            var Q0;
            {var subQ4=sQuery(id+"F49.wireOp",EDGE,"E33.left");Q0=makeQuery(id+"F49.imprint","IMPRINT",FACE,{"disambiguationData":[TD([[makeQuery(id+"F49.imprint","IMPRINT",EDGE,{"derivedFrom":subQ4}),-1.0]])]});}
            extrude(context, id + "F50", {"entities" : qUnion([Q0]), "operationType" : NewBodyOperationType.REMOVE, "oppositeDirection" : true, "depth" : 3 * mm});
        }
    });
